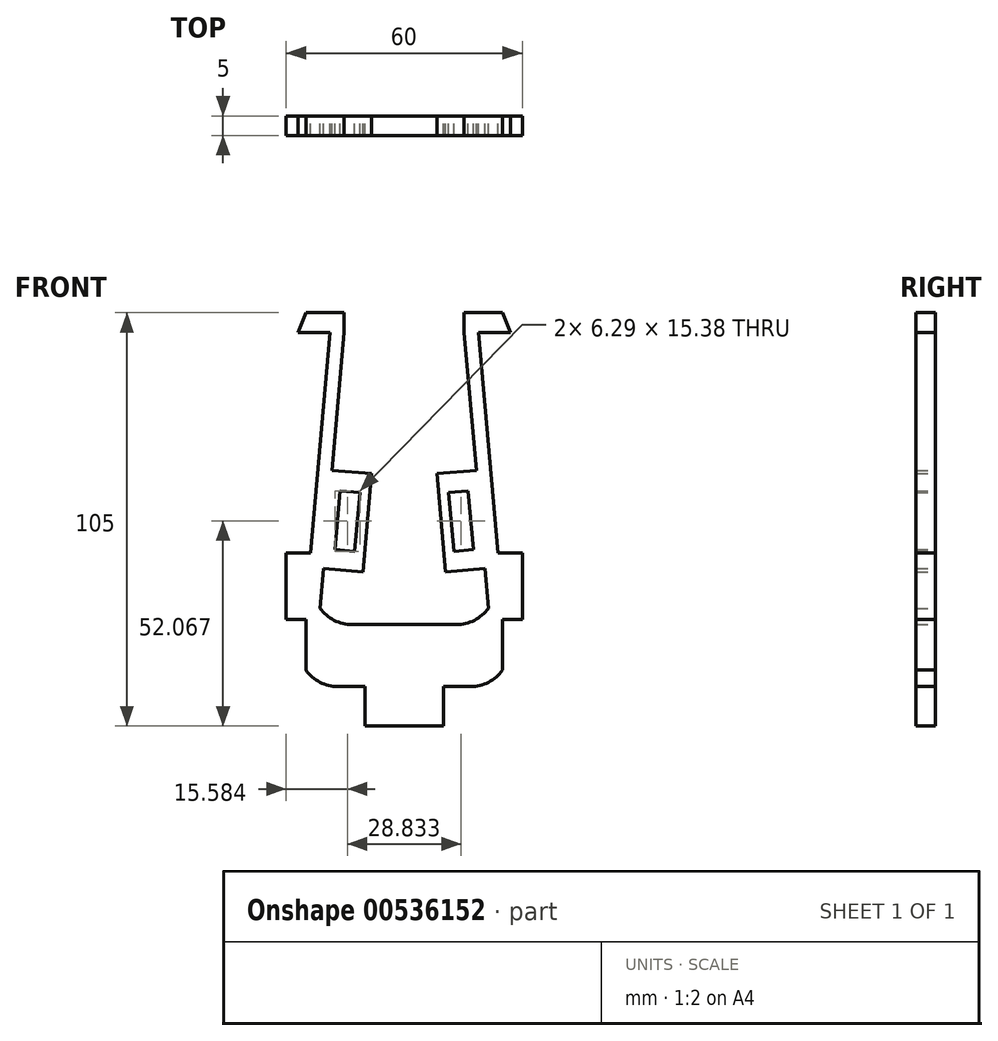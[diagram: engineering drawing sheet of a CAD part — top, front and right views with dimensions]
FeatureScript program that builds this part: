
annotation { "Feature Type Name" : "Feature", "Feature Type Description" : "" }
export const myFeature = defineFeature(function(context is Context, id is Id, definition is map)
    precondition{}
    {
        {
            var Q0;
            Q0=qCreatedBy(makeId("Front.planeOp"),FACE);
            var sketch = newSketch(context, id + "F0", { "sketchPlane" : qUnion([Q0])});
            skLineSegment(sketch, "E0", {"start": v(-16.86, -30.05) * mm, "end": v(-10, -30.05) * mm});
            skLineSegment(sketch, "E1", {"start": v(-25, 59.95) * mm, "end": v(-27, 59.95) * mm});
            skLineSegment(sketch, "E2", {"start": v(-27, 59.95) * mm, "end": v(-25, 64.95) * mm});
            skLineSegment(sketch, "E3", {"start": v(-25, 64.95) * mm, "end": v(-21, 64.95) * mm});
            skPoint(sketch, "E4.visualSharp", {"position": v(-21, -10.05) * mm});
            skArc(sketch, "E4.filletArc", {"start": v(-21.37, -10.14) * mm, "mid": v(-17.81, -13.22) * mm, "end": v(-13.24, -14.33) * mm});
            skPoint(sketch, "E5.visualSharp", {"position": v(25, -30.05) * mm});
            skPoint(sketch, "E6.visualSharp", {"position": v(-25, -30.05) * mm});
            skArc(sketch, "E6.filletArc", {"start": v(-25, -25.86) * mm, "mid": v(-21.44, -28.94) * mm, "end": v(-16.86, -30.05) * mm});
            skLineSegment(sketch, "E7", {"start": v(-21.37, -10.14) * mm, "end": v(-20.49, 0) * mm});
            skLineSegment(sketch, "E8", {"start": v(-23.77, 3.95) * mm, "end": v(-18.87, 59.95) * mm});
            skLineSegment(sketch, "E9", {"start": v(-25, -13.05) * mm, "end": v(-25, -25.86) * mm});
            skLineSegment(sketch, "E10", {"start": v(-25, 59.95) * mm, "end": v(-18.87, 59.95) * mm});
            skLineSegment(sketch, "E11", {"start": v(-21, 64.95) * mm, "end": v(-15.24, 64.95) * mm});
            skLineSegment(sketch, "E12", {"start": v(-15.24, 64.95) * mm, "end": v(-15.24, 59.95) * mm});
            skLineSegment(sketch, "E13", {"start": v(-10, -30.05) * mm, "end": v(-10, -40.05) * mm});
            skLineSegment(sketch, "E14", {"start": v(-10, -40.05) * mm, "end": v(10, -40.05) * mm});
            skLineSegment(sketch, "E15", {"start": v(10, -40.05) * mm, "end": v(10, -30.05) * mm});
            skLineSegment(sketch, "E16", {"start": v(-25, -13.05) * mm, "end": v(-30, -13.05) * mm});
            skLineSegment(sketch, "E17", {"start": v(-30, -13.05) * mm, "end": v(-30, 3.95) * mm});
            skLineSegment(sketch, "E18", {"start": v(-30, 3.95) * mm, "end": v(-23.77, 3.95) * mm});
            skPoint(sketch, "E19.orphan", {"position": v(-25, -10.14) * mm});
            skLineSegment(sketch, "E20.MirrorCS", {"start": v(10, -40.05) * mm, "end": v(-10, -40.05) * mm});
            skLineSegment(sketch, "E21.MirrorCS", {"start": v(16.86, -30.05) * mm, "end": v(10, -30.05) * mm});
            skLineSegment(sketch, "E22.MirrorCS", {"start": v(25, 59.95) * mm, "end": v(27, 59.95) * mm});
            skLineSegment(sketch, "E23.MirrorCS", {"start": v(25, 59.95) * mm, "end": v(18.87, 59.95) * mm});
            skLineSegment(sketch, "E24.MirrorCS", {"start": v(21, 64.95) * mm, "end": v(15.24, 64.95) * mm});
            skLineSegment(sketch, "E25.MirrorCS", {"start": v(25, 64.95) * mm, "end": v(21, 64.95) * mm});
            skLineSegment(sketch, "E26.MirrorCS", {"start": v(25, -13.05) * mm, "end": v(30, -13.05) * mm});
            skLineSegment(sketch, "E27.MirrorCS", {"start": v(30, 3.95) * mm, "end": v(23.77, 3.95) * mm});
            skArc(sketch, "E28.MirrorCS", {"start": v(25, -25.86) * mm, "mid": v(21.44, -28.94) * mm, "end": v(16.86, -30.05) * mm});
            skArc(sketch, "E29.MirrorCS", {"start": v(21.37, -10.14) * mm, "mid": v(17.81, -13.22) * mm, "end": v(13.24, -14.33) * mm});
            skPoint(sketch, "E30.MirrorP", {"position": v(21, -10.05) * mm});
            skLineSegment(sketch, "E31.MirrorCS", {"start": v(27, 59.95) * mm, "end": v(25, 64.95) * mm});
            skLineSegment(sketch, "E32.MirrorCS", {"start": v(30, -13.05) * mm, "end": v(30, 3.95) * mm});
            skPoint(sketch, "E33.MirrorP", {"position": v(25, -10.14) * mm});
            skLineSegment(sketch, "E34.MirrorCS", {"start": v(10, -30.05) * mm, "end": v(10, -40.05) * mm});
            skLineSegment(sketch, "E35.MirrorCS", {"start": v(15.24, 64.95) * mm, "end": v(15.24, 59.95) * mm});
            skLineSegment(sketch, "E36.MirrorCS", {"start": v(23.77, 3.95) * mm, "end": v(18.87, 59.95) * mm});
            skLineSegment(sketch, "E37.MirrorCS", {"start": v(21.37, -10.14) * mm, "end": v(20.49, 0) * mm});
            skLineSegment(sketch, "E38.MirrorCS", {"start": v(25, -13.05) * mm, "end": v(25, -25.86) * mm});
            skLineSegment(sketch, "E39", {"start": v(-13.24, -14.33) * mm, "end": v(13.24, -14.33) * mm});
            skPoint(sketch, "E40.endSnap0", {"position": v(-18.3, 24.9) * mm});
            skLineSegment(sketch, "E41", {"start": v(-8.35, 24.03) * mm, "end": v(-10.45, 0) * mm});
            skLineSegment(sketch, "E42", {"start": v(-16.25, 19.7) * mm, "end": v(-17.56, 4.76) * mm});
            skLineSegment(sketch, "E43", {"start": v(-17.56, 4.76) * mm, "end": v(-12.58, 4.33) * mm});
            skLineSegment(sketch, "E44", {"start": v(-12.58, 4.33) * mm, "end": v(-11.27, 19.27) * mm});
            skLineSegment(sketch, "E45", {"start": v(-16.25, 19.7) * mm, "end": v(-11.27, 19.27) * mm});
            skPoint(sketch, "E46.orphan", {"position": v(-11.23, 19.7) * mm});
            skLineSegment(sketch, "E47.trimOffspring", {"start": v(-18.3, 24.9) * mm, "end": v(-15.24, 59.95) * mm});
            skLineSegment(sketch, "E48", {"start": v(-18.3, 24.9) * mm, "end": v(-8.35, 24.03) * mm});
            skLineSegment(sketch, "E49", {"start": v(-20.49, 0) * mm, "end": v(-10.52, -0.87) * mm});
            skPoint(sketch, "E50.orphan", {"position": v(-8.27, 24.9) * mm});
            skLineSegment(sketch, "E51", {"start": v(-10.45, 0) * mm, "end": v(-10.52, -0.87) * mm});
            skPoint(sketch, "E52.orphan", {"position": v(-10.45, -0.88) * mm});
            skLineSegment(sketch, "E53.MirrorCS", {"start": v(20.49, 0) * mm, "end": v(10.52, -0.87) * mm});
            skLineSegment(sketch, "E54.MirrorCS", {"start": v(17.56, 4.76) * mm, "end": v(12.58, 4.33) * mm});
            skLineSegment(sketch, "E55.MirrorCS", {"start": v(16.25, 19.7) * mm, "end": v(17.56, 4.76) * mm});
            skLineSegment(sketch, "E56.MirrorCS", {"start": v(12.58, 4.33) * mm, "end": v(11.27, 19.27) * mm});
            skLineSegment(sketch, "E57.MirrorCS", {"start": v(8.35, 24.03) * mm, "end": v(10.45, 0) * mm});
            skLineSegment(sketch, "E58.MirrorCS", {"start": v(10.45, 0) * mm, "end": v(10.52, -0.87) * mm});
            skLineSegment(sketch, "E59.MirrorCS", {"start": v(18.3, 24.9) * mm, "end": v(8.35, 24.03) * mm});
            skLineSegment(sketch, "E60.MirrorCS", {"start": v(16.25, 19.7) * mm, "end": v(11.27, 19.27) * mm});
            skLineSegment(sketch, "E61.trimOffspring", {"start": v(18.3, 24.9) * mm, "end": v(15.24, 59.95) * mm});
            skSolve(sketch);
        }
        {
            var Q0;
            Q0 = qSketchRegion(id + "F0", true);
            extrude(context, id + "F1", {"entities" : qUnion([Q0]), "depth" : 5 * mm, "offsetDistance" : 25 * mm});
        }
    });
